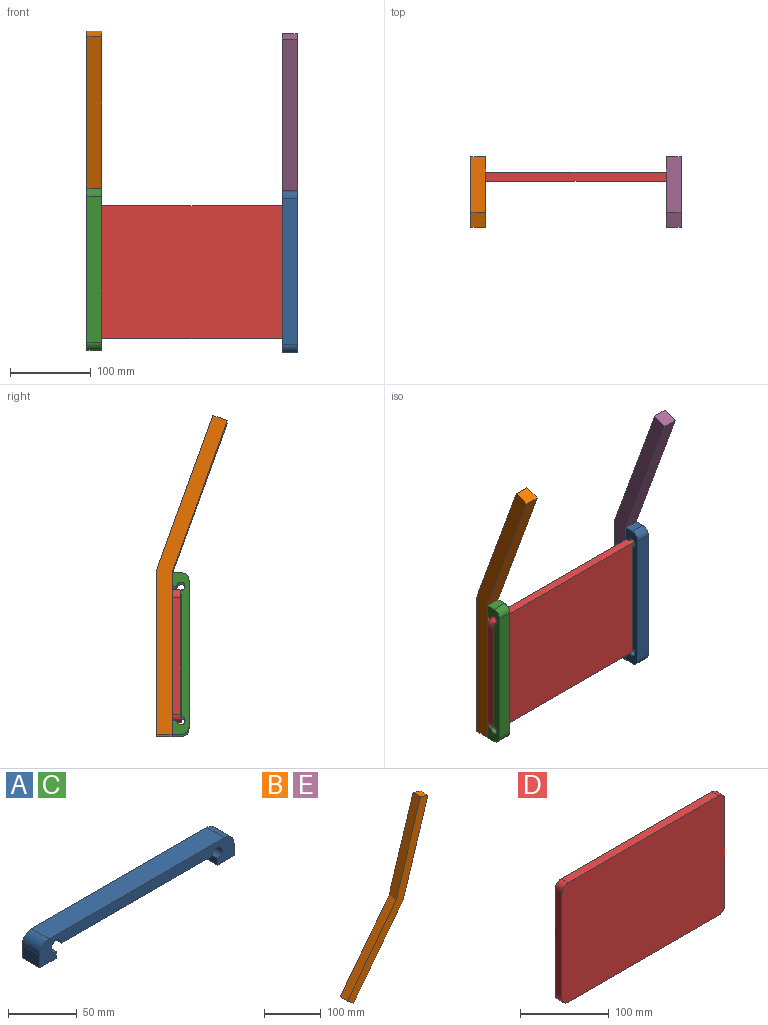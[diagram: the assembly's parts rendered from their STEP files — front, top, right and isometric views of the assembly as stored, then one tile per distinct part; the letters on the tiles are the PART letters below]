
ASSEMBLY  parts=5 mates=11
PART A: 14 faces, bbox 200x18.2x21 mm
  f0: plane 18.21x5.92mm, normal (1,0,0), area 107.8mm2, adj f6,f8,f9,f11
  f1: plane 155.84x18.21mm, normal (0,0,-1), area 2838.1mm2, adj f8,f9,f10,f11
  f2: plane 18.21x5.92mm, normal (-1,0,0), area 107.8mm2, adj f7,f8,f9,f10
  f3: plane 18.21x11.19mm, normal (1,0,0), area 203.8mm2, adj f7,f8,f9,f12
  f4: plane 180.38x18.21mm, normal (0,0,1), area 3285mm2, adj f8,f9,f12,f13
  f5: plane 18.21x11.19mm, normal (-1,0,0), area 203.8mm2, adj f6,f8,f9,f13
  f6: plane 18.21x17mm, normal (0,0,-1), area 309.6mm2, adj f0,f5,f8,f9
  f7: plane 18.21x17mm, normal (0,0,-1), area 309.6mm2, adj f2,f3,f8,f9
  f8: plane 200x21mm, normal (0,-1,0), area 2211.1mm2, adj f0,f1,f2,f3,f4,f5,f6,f7
  f9: plane 200x21mm, normal (0,1,0), area 2211.1mm2, adj f0,f1,f2,f3,f4,f5,f6,f7
  f10: cylinder r=5.08mm len=18.21mm, axis (0,-1,0), area 436mm2, adj f1,f2,f8,f9
  f11: cylinder r=5.08mm len=18.21mm, axis (0,-1,0), area 436mm2, adj f0,f1,f8,f9
  f12: cylinder r=9.81mm len=18.21mm, axis (0,1,0), area 280.7mm2, adj f3,f4,f8,f9
  f13: cylinder r=9.81mm len=18.21mm, axis (0,1,0), area 280.7mm2, adj f4,f5,f8,f9
PART B: 8 faces, bbox 199.7x18.2x361.2 mm
  f0: plane 161.46x123.64mm, normal (0.79,0,-0.61), area 3703.5mm2, adj f1,f5,f6,f7
  f1: plane 194.01x60.96mm, normal (0.95,0,-0.3), area 3703.5mm2, adj f0,f2,f6,f7
  f2: plane 18.21x18.17mm, normal (0.3,0,0.95), area 346.9mm2, adj f1,f3,f6,f7
  f3: plane 190.8x59.95mm, normal (-0.95,0,0.3), area 3642.4mm2, adj f2,f4,f6,f7
  f4: plane 158.79x121.6mm, normal (-0.79,0,0.61), area 3642.4mm2, adj f3,f5,f6,f7
  f5: plane 18.21x15.12mm, normal (-0.61,0,-0.79), area 346.9mm2, adj f0,f4,f6,f7
  f6: plane 361.17x199.73mm, normal (0,-1,0), area 7684mm2, adj f0,f1,f2,f3,f4,f5
  f7: plane 361.17x199.73mm, normal (0,1,0), area 7684mm2, adj f0,f1,f2,f3,f4,f5
PART C: same geometry as A
PART D: 10 faces, bbox 260x11.1x165 mm
  f0: plane 240x11.1mm, normal (0,0,-1), area 2664mm2, adj f4,f5,f6,f9
  f1: plane 145x11.1mm, normal (1,0,0), area 1609.5mm2, adj f4,f5,f6,f7
  f2: plane 240x11.1mm, normal (0,0,1), area 2664mm2, adj f4,f5,f7,f8
  f3: plane 145x11.1mm, normal (-1,0,0), area 1609.5mm2, adj f4,f5,f8,f9
  f4: plane 260x165mm, normal (0,-1,0), area 42814.2mm2, adj f0,f1,f2,f3,f6,f7,f8,f9
  f5: plane 260x165mm, normal (0,1,0), area 42814.2mm2, adj f0,f1,f2,f3,f6,f7,f8,f9
  f6: cylinder r=10mm len=11.1mm, axis (0,-1,0), area 174.4mm2, adj f0,f1,f4,f5
  f7: cylinder r=10mm len=11.1mm, axis (0,1,0), area 174.4mm2, adj f1,f2,f4,f5
  f8: cylinder r=10mm len=11.1mm, axis (0,-1,0), area 174.4mm2, adj f2,f3,f4,f5
  f9: cylinder r=10mm len=11.1mm, axis (0,1,0), area 174.4mm2, adj f0,f3,f4,f5
PART E: same geometry as B
PLACE A rot(axis=(0.58,0.58,-0.58),120deg) t=(55.13,-23.67,119.58)mm
PLACE B rot(axis=(0.7,0.7,-0.11),167.7deg) t=(-186.66,-12.67,139.62)mm
PLACE C rot(axis=(0.58,-0.58,0.58),120deg) t=(-204.87,-23.67,-43.38)mm
PLACE D t=(-74.87,-12.67,36.08)mm fixed
PLACE E rot(axis=(0.31,-0.31,0.9),95.9deg) t=(36.92,-12.67,136.58)mm
MATE planar B.f3 <-> D.f5  axis (0,-1,0) through (-195.76,-12.67,39.62)mm
MATE planar B.f3 <-> C.f6  axis (0,-1,0) through (-195.76,-12.67,-60.38)mm
MATE planar A.f3 <-> E.f5  axis (0,0,-1) through (46.02,-18.26,-63.42)mm
MATE planar D.f3 <-> B.f6  axis (-1,0,0) through (-204.87,-18.22,36.08)mm
MATE planar E.f4 <-> D.f5  axis (0,-1,0) through (46.02,-12.67,36.58)mm
MATE planar E.f6 <-> A.f9  axis (1,0,0) through (55.13,-20.36,135.23)mm
MATE planar E.f4 <-> A.f7  axis (0,-1,0) through (46.02,-12.67,36.58)mm
MATE planar C.f5 <-> B.f2  axis (0,0,-1) through (-195.76,-18.26,-60.38)mm
MATE planar A.f2 <-> D.f0  axis (0,0,1) through (46.02,-15.63,-46.42)mm
MATE planar C.f9 <-> B.f6  axis (-1,0,0) through (-204.87,-27.08,39.62)mm
MATE planar E.f6 <-> D.f1  axis (1,0,0) through (55.13,-20.36,135.23)mm
